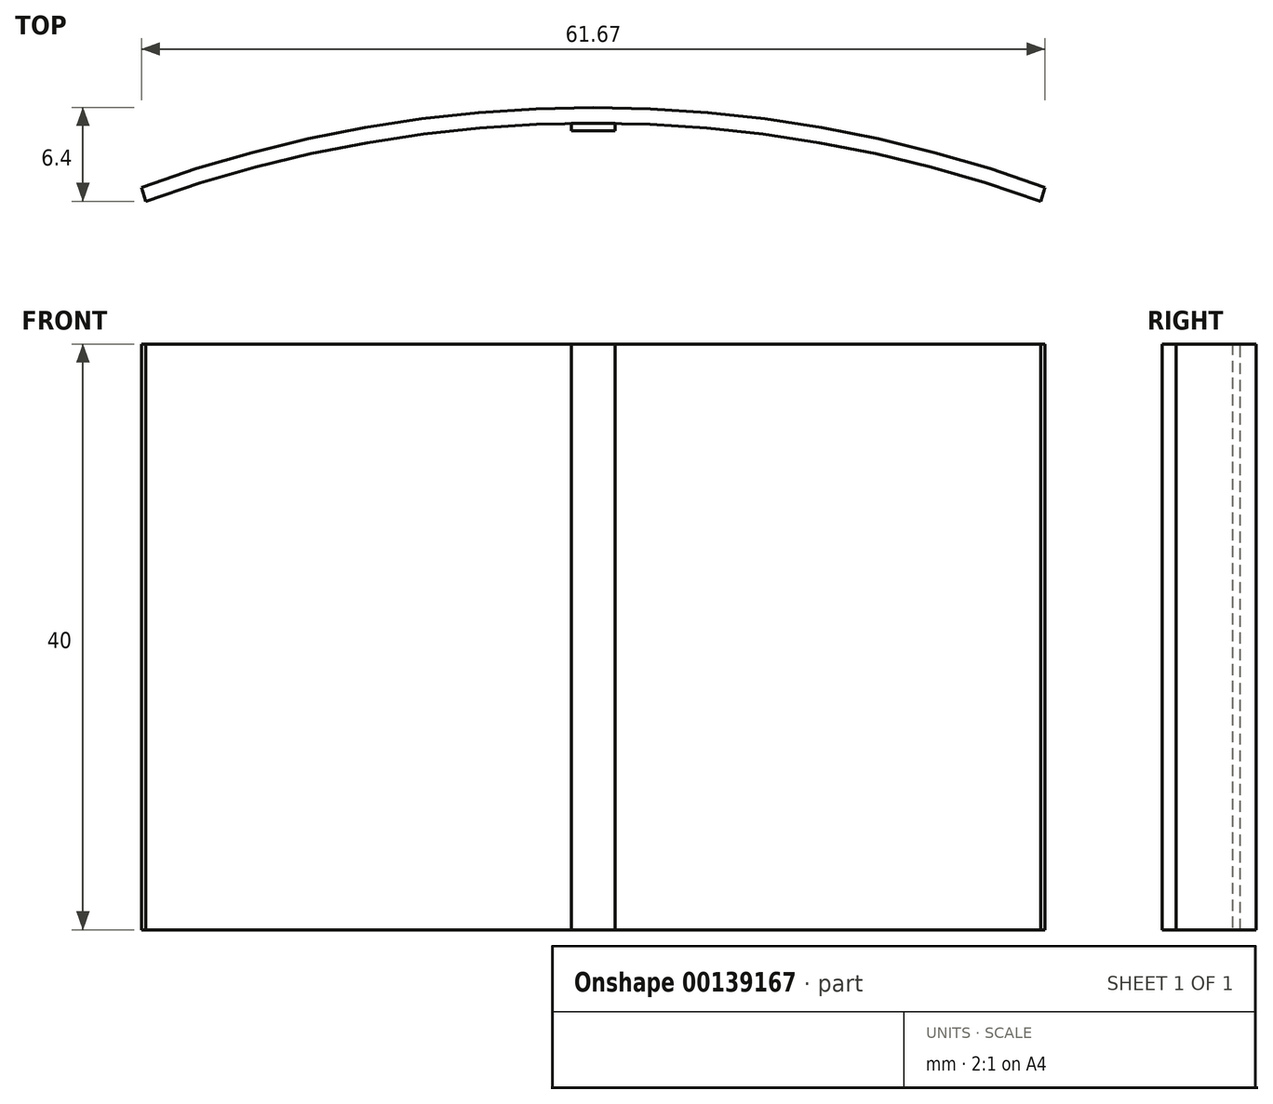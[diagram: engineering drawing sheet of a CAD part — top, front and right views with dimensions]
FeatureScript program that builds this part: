
annotation { "Feature Type Name" : "Feature", "Feature Type Description" : "" }
export const myFeature = defineFeature(function(context is Context, id is Id, definition is map)
    precondition{}
    {
        {
            var Q0;
            Q0=qCreatedBy(makeId("Top.planeOp"),FACE);
            var sketch = newSketch(context, id + "F0", { "sketchPlane" : qUnion([Q0])});
            skLineSegment(sketch, "E0", {"start": v(0, 0) * mm, "end": v(61.07, 0) * mm});
            skArc(sketch, "E1", {"start": v(61.07, 0) * mm, "mid": v(30.53, 5.33) * mm, "end": v(0, 0) * mm});
            skLineSegment(sketch, "E2", {"start": v(0, 0) * mm, "end": v(-0.3, 0.95) * mm});
            skLineSegment(sketch, "E3", {"start": v(0, 0) * mm, "end": v(7, 2.2) * mm});
            skLineSegment(sketch, "E4", {"start": v(61.07, 0) * mm, "end": v(54.92, 1.97) * mm});
            skLineSegment(sketch, "E5", {"start": v(61.07, 0) * mm, "end": v(61.37, 0.95) * mm});
            skArc(sketch, "E6", {"start": v(61.37, 0.95) * mm, "mid": v(30.54, 6.4) * mm, "end": v(-0.3, 0.95) * mm});
            skLineSegment(sketch, "E7", {"start": v(32.03, 5.32) * mm, "end": v(32.03, 4.8) * mm});
            skLineSegment(sketch, "E8", {"start": v(32.03, 4.8) * mm, "end": v(29.03, 4.8) * mm});
            skPoint(sketch, "E8.endSnap0", {"position": v(29.03, 5.32) * mm});
            skLineSegment(sketch, "E9", {"start": v(29.03, 4.8) * mm, "end": v(29.03, 5.32) * mm});
            skLineSegment(sketch, "E10", {"start": v(29.03, 4.8) * mm, "end": v(0, 0) * mm});
            skLineSegment(sketch, "E11", {"start": v(32.03, 4.8) * mm, "end": v(61.07, 0) * mm});
            skLineSegment(sketch, "E12", {"start": v(32.03, 5.32) * mm, "end": v(29.03, 5.32) * mm});
            skLineSegment(sketch, "E13", {"start": v(61.07, 0) * mm, "end": v(0, -1.57) * mm});
            skLineSegment(sketch, "E14", {"start": v(0, -1.57) * mm, "end": v(0, 0) * mm});
            skSolve(sketch);
        }
        {
            var Q0;
            {var subQ0=sQuery(id+"F0.wireOp",EDGE,"E2");Q0=makeQuery(id+"F0.imprint","IMPRINT",FACE,{"disambiguationData":[TD([[makeQuery(id+"F0.imprint","IMPRINT",EDGE,{"derivedFrom":subQ0}),-1.0]])]});}
            var Q1;
            {var subQ0=sQuery(id+"F0.wireOp",EDGE,"E7");Q1=makeQuery(id+"F0.imprint","IMPRINT",FACE,{"disambiguationData":[TD([[makeQuery(id+"F0.imprint","IMPRINT",EDGE,{"derivedFrom":subQ0}),-1.0]])]});}
            extrude(context, id + "F1", {"entities" : qUnion([Q0, Q1]), "depth" : 40 * mm, "hasDraft" : true, "draftAngle" : 0 * degree});
        }
    });
